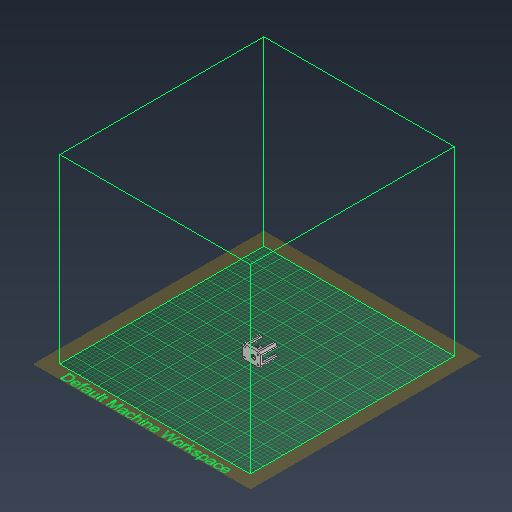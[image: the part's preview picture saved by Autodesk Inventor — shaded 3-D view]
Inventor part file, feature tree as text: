
AUTODESK INVENTOR PART (.ipt)
format: ipt  version: 2021 (Build 250183000, 183)  size: 529,408 bytes
history: native  units: mm
features: extrude x20, sketch x16, fillet x2
ambient origin geometry x8: Origin, YZ Plane, XZ Plane, XY Plane, X Axis, Y Axis, Z Axis, Center Point
bodies: Volumenkörper1 (feature_tree)
feature tree (38):
  extrude  "Extrusion1"  Depth=29.5mm
  sketch  "Skizze2"  dims[d2=6.0mm d3=0.0mm d12=3.5mm]
  sketch  "Skizze3"  dims[d13=5.0mm d14=5.0mm]
  extrude  "Extrusion2"  Depth=3.5mm
  extrude  "Extrusion3"  Depth=5.0mm
  extrude  "Extrusion4"  Depth=3.5mm
  extrude  "Extrusion5"  Depth=3.5mm
  extrude  "Extrusion6"  Depth=5.0mm
  extrude  "Extrusion7"  Depth=2.0mm
  fillet  "Rundung1"  Radius=5.0mm
  fillet  "Rundung2"  Radius=2.0mm
  sketch  "Skizze5"  dims[d17=5.0mm d18=3.5mm]
  extrude  "Extrusion8"  Depth=2.0mm
  extrude  "Extrusion9"  Depth=7.75mm
  extrude  "Extrusion10"  Depth=7.75mm
  extrude  "Extrusion11"  Depth=14.5mm
  extrude  "Extrusion14"  Depth=7.75mm
  extrude  "Extrusion15"  Depth=7.75mm
  extrude  "Extrusion16"  Depth=7.75mm
  sketch  "Skizze15"  dims[d35=7.75mm d36=7.75mm]
  sketch  "Skizze16"  dims[d37=7.75mm d38=7.75mm]
  extrude  "Extrusion17"  Depth=4.0mm TaperAngle=0.0deg
  extrude  "Extrusion18"  Depth=4.0mm TaperAngle=0.0deg
  extrude  "Extrusion19"  Depth=31.5mm TaperAngle=0.0deg
  sketch  "Skizze18"  dims[d41=31.5mm d42=0.0mm d43=4.0mm d44=0.0mm]
  extrude  "Extrusion20"  Depth=31.5mm TaperAngle=0.0deg
  extrude  "Extrusion21"  Depth=20.0mm TaperAngle=0.0deg
  extrude  "Extrusion22"  Depth=3.5mm
  sketch  "Skizze1"  dims[d0=39.5mm d1=29.5mm]
  sketch  "Skizze4"  dims[d15=3.5mm d16=5.0mm]
  sketch  "Skizze6"  dims[d19=5.0mm d20=5.0mm]
  sketch  "Skizze7"  dims[d21=3.5mm d22=5.0mm d23=5.0mm d24=2.0mm]
  sketch  "Skizze8"  dims[d25=2.0mm d28=2.0mm]
  sketch  "Skizze12"  dims[d29=2.0mm d30=7.75mm]
  sketch  "Skizze13"  dims[d31=7.75mm d32=15.4mm]
  sketch  "Skizze14"  dims[d33=14.5mm d34=14.75mm]
  sketch  "Skizze17"  dims[d39=7.75mm d40=7.75mm]
  sketch  "Skizze19"  dims[d45=10.6mm d46=4.0mm d47=0.0mm d48=31.5mm d49=0.0mm d50=31.5mm d51=0.0mm d52=20.0mm d53=0.0mm d54=3.5mm d55=4.0mm d56=16.5mm d57=3.5mm d58=7.75mm d59=7.75mm d60=3.5mm d61=20.0mm d62=0.0mm d63=20.0mm d64=0.0mm d65=14.0mm d66=16.5mm d67=7.25mm d68=3.5mm d69=20.0mm d70=0.0mm d71=14.0mm d72=16.5mm d73=7.25mm d74=3.5mm d75=20.0mm d76=0.0mm d86=4.0mm d87=0.0mm d88=4.0mm d89=0.0mm d90=10.0mm d91=0.0mm d92=10.0mm d93=0.0mm d94=10.0mm d95=0.0mm d96=0.5mm d97=0.0mm d98=0.5mm d99=0.0mm d100=0.5mm d101=0.0mm d102=0.5mm d103=0.0mm]
